# Revit family: FU Chair_Sandler_KERN 0110
name_source: partatom
category: Furniture
units: mm (PartAtom-declared; Revit-internal decimal feet)

## family parameters
Always vertical = Yes
Cut with Voids When Loaded = No
OmniClass Number = 23.40.20.00
OmniClass Title = General Furniture and Specialties
Render Appearance Source = Family Geometry
Room Calculation Point = No
Shared = No
Work Plane-Based = No

## types (1)
- Kern 0110
    Default Elevation = 0 mm  [stored 0 ft]
    Depth = 710 mm  [stored 2.3294 ft]
    Description = Backless square seating element in the Kern modular series. Epoxy-painted legs. 99% recyclable.
    Height = 740 mm  [stored 2.42782 ft]
    Manufacturer = Sandler
    Model = Kern 0110
    URL = https://www.sandlerseating.com
    Width = 710 mm  [stored 2.3294 ft]

note: [stored X ft] marks values corroborated as IEEE doubles in the binary element streams (Revit-internal decimal feet)

## geometry (parser evidence)
native form markers: Sweep x7
no freeform markers — native parametric forms only
